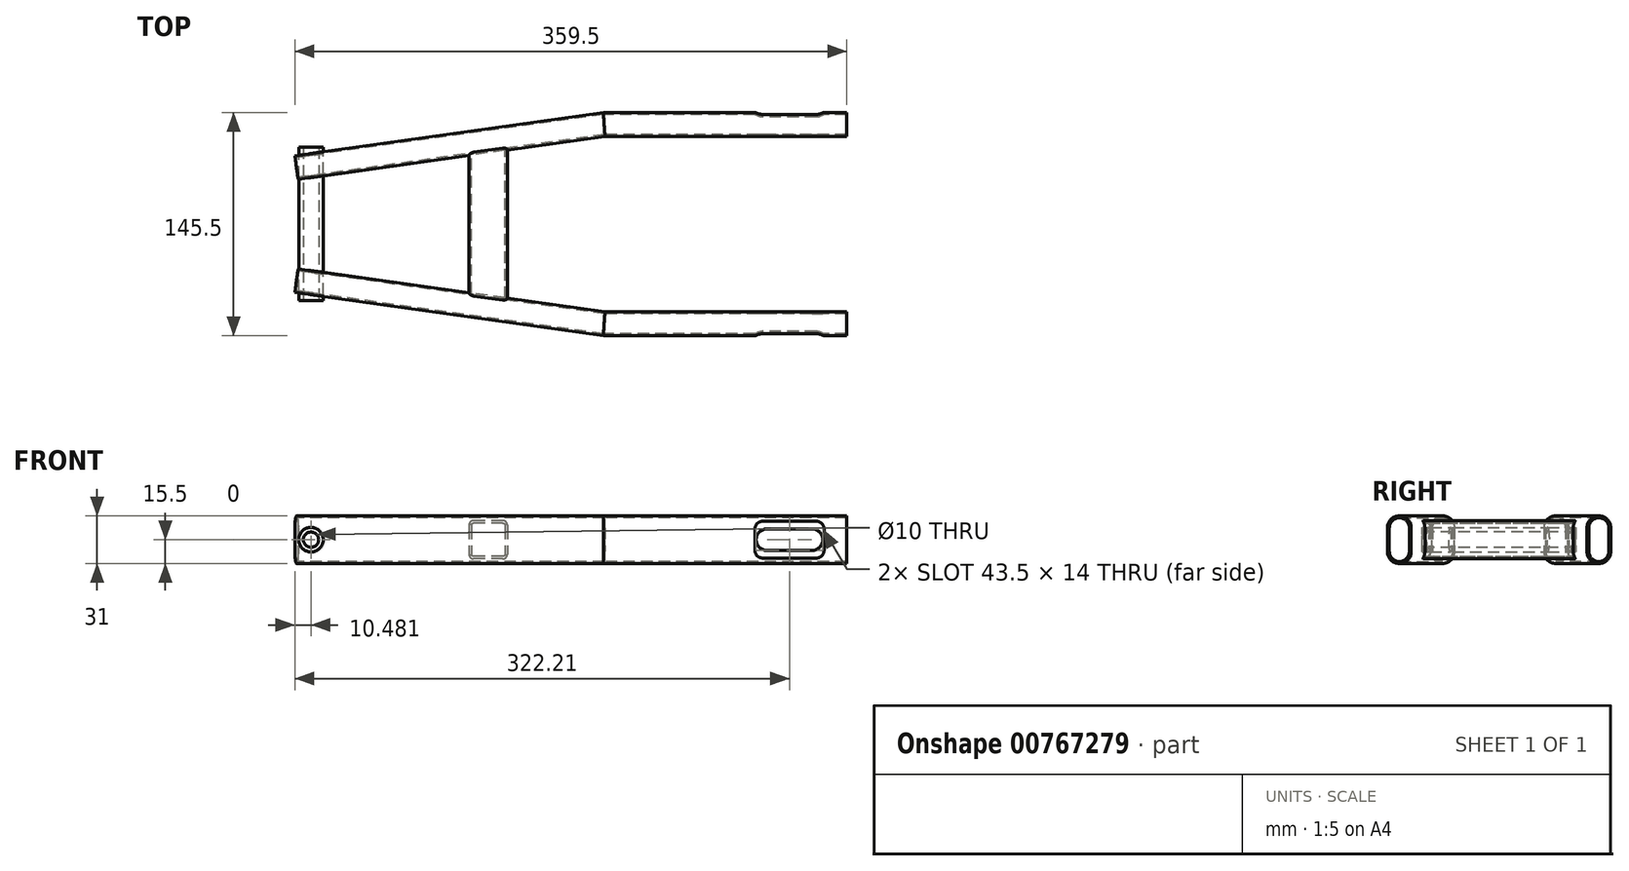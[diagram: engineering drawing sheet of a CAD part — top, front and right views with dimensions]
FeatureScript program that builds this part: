
annotation { "Feature Type Name" : "Feature", "Feature Type Description" : "" }
export const myFeature = defineFeature(function(context is Context, id is Id, definition is map)
    precondition{}
    {
        {
            var Q0;
            Q0=qCreatedBy(makeId("Top.planeOp"),FACE);
            var sketch = newSketch(context, id + "F0", { "sketchPlane" : qUnion([Q0])});
            skLineSegment(sketch, "E0", {"start": v(0, 65) * mm, "end": v(-158.03, 65) * mm});
            skLineSegment(sketch, "E1", {"start": v(-158.03, 65) * mm, "end": v(-358.42, 36.84) * mm});
            skSolve(sketch);
        }
        {
            var Q0;
            Q0=qCreatedBy(makeId("Right.planeOp"),FACE);
            var sketch = newSketch(context, id + "F1", { "sketchPlane" : qUnion([Q0])});
            skLineSegment(sketch, "E2.left", {"start": v(57.25, 7.75) * mm, "end": v(57.25, -7.75) * mm});
            skLineSegment(sketch, "E2.right", {"start": v(72.75, 7.75) * mm, "end": v(72.75, -7.75) * mm});
            skPoint(sketch, "E2.middle", {"position": v(65, 0) * mm});
            skArc(sketch, "E3", {"start": v(57.25, 7.75) * mm, "mid": v(65, 15.5) * mm, "end": v(72.75, 7.75) * mm});
            skArc(sketch, "E4.MirrorCS", {"start": v(57.25, -7.75) * mm, "mid": v(65, -15.5) * mm, "end": v(72.75, -7.75) * mm});
            skLineSegment(sketch, "E5.0", {"start": v(58.45, 7.75) * mm, "end": v(58.45, -7.75) * mm});
            skLineSegment(sketch, "E6.0", {"start": v(71.55, 7.75) * mm, "end": v(71.55, -7.75) * mm});
            skArc(sketch, "E7.0", {"start": v(58.45, 7.75) * mm, "mid": v(65, 14.3) * mm, "end": v(71.55, 7.75) * mm});
            skArc(sketch, "E8.0", {"start": v(58.45, -7.75) * mm, "mid": v(65, -14.3) * mm, "end": v(71.55, -7.75) * mm});
            skSolve(sketch);
        }
        {
            var Q0;
            Q0 = qSketchRegion(id + "F1", true);
            var Q1;
            Q1 = qConstructionFilter(qBodyType(qCreatedBy(id + "F0" ,EDGE), BodyType.WIRE), ConstructionObject.NO);
            sweep(context, id + "F2", {"profiles" : qUnion([Q0]), "path" : qUnion([Q1])});
        }
        {
            var Q0;
            Q0=makeQuery(id+"F2.opSweep","SWEPT_BODY",BODY,{"disambiguationData":[OSD([sQuery(id+"F0.wireOp",EDGE,"E1"),sQuery(id+"F1.wireOp",EDGE,"E2.left"),sQuery(id+"F1.wireOp",EDGE,"E2.right"),sQuery(id+"F1.wireOp",EDGE,"E3"),sQuery(id+"F1.wireOp",EDGE,"E4.MirrorCS"),sQuery(id+"F1.wireOp",EDGE,"E5.0"),sQuery(id+"F1.wireOp",EDGE,"E6.0"),sQuery(id+"F1.wireOp",EDGE,"E7.0"),sQuery(id+"F1.wireOp",EDGE,"E8.0")])]});
            var Q1;
            Q1=qCreatedBy(makeId("Front.planeOp"),FACE);
            mirror(context, id + "F3", {"entities" : qUnion([Q0]), "mirrorPlane" : qUnion([Q1])});
        }
        {
            var Q0;
            Q0=makeQuery(id+"F3.opPattern","COPY",FACE,{"derivedFrom":makeQuery(id+"F2.opSweep","SWEPT_FACE",FACE,{"disambiguationData":[OSD([sQuery(id+"F0.wireOp",EDGE,"E0"),sQuery(id+"F1.wireOp",EDGE,"E2.right")])]}),"instanceName":"1"});
            var sketch = newSketch(context, id + "F4", { "sketchPlane" : qUnion([Q0])});
            skLineSegment(sketch, "E9.bottom", {"start": v(-22.54, -7) * mm, "end": v(-52.04, -7) * mm});
            skLineSegment(sketch, "E9.top", {"start": v(-22.54, 7) * mm, "end": v(-52.04, 7) * mm});
            skPoint(sketch, "E9.middle", {"position": v(-37.3, 0) * mm});
            skArc(sketch, "E10", {"start": v(-22.54, 7) * mm, "mid": v(-15.54, 0) * mm, "end": v(-22.54, -7) * mm});
            skArc(sketch, "E11", {"start": v(-52.04, 7) * mm, "mid": v(-59.04, 0) * mm, "end": v(-52.04, -7) * mm});
            skSolve(sketch);
        }
        {
            var Q0;
            Q0 = qSketchRegion(id + "F4", true);
            extrude(context, id + "F5", {"entities" : qUnion([Q0]), "operationType" : NewBodyOperationType.REMOVE, "endBound" : BoundingType.SYMMETRIC, "oppositeDirection" : true, "depth" : 5000 * mm, "offsetDistance" : 25 * mm});
        }
        {
            var Q0;
            Q0=qCreatedBy(makeId("Front.planeOp"),FACE);
            var sketch = newSketch(context, id + "F6", { "sketchPlane" : qUnion([Q0])});
            skCircle(sketch, "E12", {"center": v(-349.02, 0) * mm, "radius": 8 * mm});
            skSolve(sketch);
        }
        {
            var Q0;
            Q0=makeQuery(id+"F6.imprint","IMPRINT",FACE,{"disambiguationData":[TD([[makeQuery(id+"F6.imprint","IMPRINT",EDGE,{"derivedFrom":sQuery(id+"F6.wireOp",EDGE,"E12")}),1.0]])]});
            extrude(context, id + "F7", {"entities" : qUnion([Q0]), "operationType" : NewBodyOperationType.ADD, "endBound" : BoundingType.SYMMETRIC, "depth" : 100 * mm, "offsetDistance" : 25 * mm});
        }
        {
            var Q0;
            Q0=qCreatedBy(makeId("Front.planeOp"),FACE);
            var sketch = newSketch(context, id + "F8", { "sketchPlane" : qUnion([Q0])});
            skLineSegment(sketch, "E13.bottom", {"start": v(-221.08, -12.5) * mm, "end": v(-246.08, -12.5) * mm});
            skLineSegment(sketch, "E13.top", {"start": v(-221.08, 12.5) * mm, "end": v(-246.08, 12.5) * mm});
            skLineSegment(sketch, "E13.left", {"start": v(-221.08, -12.5) * mm, "end": v(-221.08, 12.5) * mm});
            skLineSegment(sketch, "E13.right", {"start": v(-246.08, -12.5) * mm, "end": v(-246.08, 12.5) * mm});
            skPoint(sketch, "E13.middle", {"position": v(-233.58, 0) * mm});
            skLineSegment(sketch, "E14.0", {"start": v(-224.08, 10.9) * mm, "end": v(-243.08, 10.9) * mm});
            skLineSegment(sketch, "E15.0", {"start": v(-222.68, -9.5) * mm, "end": v(-222.68, 9.5) * mm});
            skLineSegment(sketch, "E16.0", {"start": v(-224.08, -10.9) * mm, "end": v(-243.08, -10.9) * mm});
            skLineSegment(sketch, "E17.0", {"start": v(-244.48, -9.5) * mm, "end": v(-244.48, 9.5) * mm});
            skArc(sketch, "E18.filletArc", {"start": v(-243.08, 10.9) * mm, "mid": v(-244.07, 10.49) * mm, "end": v(-244.48, 9.5) * mm});
            skArc(sketch, "E19.filletArc", {"start": v(-222.68, 9.5) * mm, "mid": v(-223.09, 10.49) * mm, "end": v(-224.08, 10.9) * mm});
            skArc(sketch, "E20.filletArc", {"start": v(-224.08, -10.9) * mm, "mid": v(-223.09, -10.49) * mm, "end": v(-222.68, -9.5) * mm});
            skArc(sketch, "E21.filletArc", {"start": v(-244.48, -9.5) * mm, "mid": v(-244.07, -10.49) * mm, "end": v(-243.08, -10.9) * mm});
            skSolve(sketch);
        }
        {
            var Q0;
            Q0=makeQuery(id+"F4.imprint","IMPRINT",FACE,{"disambiguationData":[TD([[makeQuery(id+"F4.imprint","IMPRINT",EDGE,{"derivedFrom":sQuery(id+"F4.wireOp",EDGE,"E9.bottom")}),-1.0]])]});
            var sketch = newSketch(context, id + "F9", { "sketchPlane" : qUnion([Q0])});
            skLineSegment(sketch, "E22.bottom", {"start": v(-19.76, -12) * mm, "end": v(-54.76, -12) * mm});
            skLineSegment(sketch, "E22.top", {"start": v(-19.76, 12) * mm, "end": v(-54.76, 12) * mm});
            skLineSegment(sketch, "E22.left", {"start": v(-14.76, -7) * mm, "end": v(-14.76, 7) * mm});
            skLineSegment(sketch, "E22.right", {"start": v(-59.76, -7) * mm, "end": v(-59.76, 7) * mm});
            skPoint(sketch, "E22.middle", {"position": v(-37.26, 0) * mm});
            skPoint(sketch, "E23.visualSharp", {"position": v(-59.76, 12) * mm});
            skArc(sketch, "E23.filletArc", {"start": v(-54.76, 12) * mm, "mid": v(-58.3, 10.54) * mm, "end": v(-59.76, 7) * mm});
            skPoint(sketch, "E24.visualSharp", {"position": v(-59.76, -12) * mm});
            skArc(sketch, "E24.filletArc", {"start": v(-59.76, -7) * mm, "mid": v(-58.3, -10.54) * mm, "end": v(-54.76, -12) * mm});
            skPoint(sketch, "E25.visualSharp", {"position": v(-14.76, 12) * mm});
            skArc(sketch, "E25.filletArc", {"start": v(-14.76, 7) * mm, "mid": v(-16.22, 10.54) * mm, "end": v(-19.76, 12) * mm});
            skPoint(sketch, "E26.visualSharp", {"position": v(-14.76, -12) * mm});
            skArc(sketch, "E26.filletArc", {"start": v(-19.76, -12) * mm, "mid": v(-16.22, -10.54) * mm, "end": v(-14.76, -7) * mm});
            skSolve(sketch);
        }
        {
            var Q0;
            Q0=makeQuery(id+"F7.opExtrude","CAP_FACE",FACE,{"disambiguationData":[OSD([sQuery(id+"F6.wireOp",EDGE,"E12")])],"isStart":false});
            var sketch = newSketch(context, id + "F10", { "sketchPlane" : qUnion([Q0])});
            skCircle(sketch, "E27", {"center": v(-349.02, 0) * mm, "radius": 5 * mm});
            skSolve(sketch);
        }
        {
            var Q0;
            Q0=makeQuery(id+"F10.imprint","IMPRINT",FACE,{"disambiguationData":[TD([[makeQuery(id+"F10.imprint","IMPRINT",EDGE,{"derivedFrom":sQuery(id+"F10.wireOp",EDGE,"E27")}),1.0]])]});
            extrude(context, id + "F11", {"entities" : qUnion([Q0]), "operationType" : NewBodyOperationType.REMOVE, "endBound" : BoundingType.THROUGH_ALL, "oppositeDirection" : true, "depth" : 25 * mm, "offsetDistance" : 25 * mm});
        }
        {
            var Q0;
            Q0=makeQuery(id+"F9.imprint","IMPRINT",FACE,{"disambiguationData":[TD([[makeQuery(id+"F9.imprint","IMPRINT",EDGE,{"derivedFrom":sQuery(id+"F9.wireOp",EDGE,"E22.bottom")}),-1.0]])]});
            extrude(context, id + "F12", {"entities" : qUnion([Q0]), "operationType" : NewBodyOperationType.REMOVE, "oppositeDirection" : true, "depth" : 3 * mm, "offsetDistance" : 25 * mm});
        }
        {
            var Q0;
            Q0=makeQuery(id+"F8.imprint","IMPRINT",FACE,{"disambiguationData":[TD([[makeQuery(id+"F8.imprint","IMPRINT",EDGE,{"derivedFrom":sQuery(id+"F8.wireOp",EDGE,"E13.bottom")}),-1.0]])]});
            var Q1;
            Q1=makeQuery(id+"F2.opSweep","SWEPT_BODY",BODY,{"disambiguationData":[OSD([sQuery(id+"F0.wireOp",EDGE,"E1"),sQuery(id+"F1.wireOp",EDGE,"E2.left"),sQuery(id+"F1.wireOp",EDGE,"E2.right"),sQuery(id+"F1.wireOp",EDGE,"E3"),sQuery(id+"F1.wireOp",EDGE,"E4.MirrorCS"),sQuery(id+"F1.wireOp",EDGE,"E5.0"),sQuery(id+"F1.wireOp",EDGE,"E6.0"),sQuery(id+"F1.wireOp",EDGE,"E7.0"),sQuery(id+"F1.wireOp",EDGE,"E8.0")])]});
            extrude(context, id + "F13", {"entities" : qUnion([Q0]), "operationType" : NewBodyOperationType.ADD, "endBound" : BoundingType.UP_TO_BODY, "depth" : 50 * mm, "endBoundEntityBody" : qUnion([Q1]), "offsetDistance" : 25 * mm});
        }
        {
            var Q0;
            Q0=makeQuery(id+"F13.opExtrude","SWEPT_EDGE",EDGE,{"disambiguationData":[OSD([sQuery(id+"F8.wireOp",EDGE,"E13.top"),sQuery(id+"F8.wireOp",EDGE,"E13.left")])]});
            var Q1;
            Q1=makeQuery(id+"F13.opExtrude","SWEPT_EDGE",EDGE,{"disambiguationData":[OSD([sQuery(id+"F8.wireOp",EDGE,"E13.top"),sQuery(id+"F8.wireOp",EDGE,"E13.right")])]});
            var Q2;
            Q2=makeQuery(id+"F13.opExtrude","SWEPT_EDGE",EDGE,{"disambiguationData":[OSD([sQuery(id+"F8.wireOp",EDGE,"E13.bottom"),sQuery(id+"F8.wireOp",EDGE,"E13.left")])]});
            var Q3;
            Q3=makeQuery(id+"F13.opExtrude","SWEPT_EDGE",EDGE,{"disambiguationData":[OSD([sQuery(id+"F8.wireOp",EDGE,"E13.bottom"),sQuery(id+"F8.wireOp",EDGE,"E13.right")])]});
            fillet(context, id + "F14", {"entities" : qUnion([Q0, Q1, Q2, Q3]), "radius" : 3 * mm, "tangentPropagation" : true, "allowEdgeOverflow" : false});
        }
        {
            var Q0;
            Q0=makeQuery(id+"F2.opSweep","SWEPT_BODY",BODY,{"disambiguationData":[OSD([sQuery(id+"F0.wireOp",EDGE,"E1"),sQuery(id+"F1.wireOp",EDGE,"E2.left"),sQuery(id+"F1.wireOp",EDGE,"E2.right"),sQuery(id+"F1.wireOp",EDGE,"E3"),sQuery(id+"F1.wireOp",EDGE,"E4.MirrorCS"),sQuery(id+"F1.wireOp",EDGE,"E5.0"),sQuery(id+"F1.wireOp",EDGE,"E6.0"),sQuery(id+"F1.wireOp",EDGE,"E7.0"),sQuery(id+"F1.wireOp",EDGE,"E8.0")])]});
            var Q1;
            Q1=qCreatedBy(makeId("Front.planeOp"),FACE);
            mirror(context, id + "F15", {"operationType" : NewBodyOperationType.ADD, "entities" : qUnion([Q0]), "mirrorPlane" : qUnion([Q1])});
        }
        {
            var Q0;
            Q0=makeQuery(id+"F9.imprint","IMPRINT",FACE,{"disambiguationData":[TD([[makeQuery(id+"F9.imprint","IMPRINT",EDGE,{"derivedFrom":sQuery(id+"F9.wireOp",EDGE,"E22.bottom")}),-1.0]])]});
            extrude(context, id + "F16", {"entities" : qUnion([Q0]), "operationType" : NewBodyOperationType.REMOVE, "oppositeDirection" : true, "depth" : 3 * mm, "offsetDistance" : 25 * mm});
        }
        {
            var Q0;
            Q0=makeQuery(id+"F2.opSweep","SWEPT_FACE",FACE,{"disambiguationData":[OSD([sQuery(id+"F0.wireOp",EDGE,"E0"),sQuery(id+"F1.wireOp",EDGE,"E2.right")])]});
            var sketch = newSketch(context, id + "F17", { "sketchPlane" : qUnion([Q0])});
            skLineSegment(sketch, "E28.bottom", {"start": v(54.76, 12) * mm, "end": v(19.76, 12) * mm});
            skLineSegment(sketch, "E28.top", {"start": v(54.76, -12) * mm, "end": v(19.76, -12) * mm});
            skLineSegment(sketch, "E28.left", {"start": v(59.76, 7) * mm, "end": v(59.76, -7) * mm});
            skLineSegment(sketch, "E28.right", {"start": v(14.76, 7) * mm, "end": v(14.76, -7) * mm});
            skPoint(sketch, "E28.middle", {"position": v(37.26, 0) * mm});
            skPoint(sketch, "E29.visualSharp", {"position": v(14.76, 12) * mm});
            skArc(sketch, "E29.filletArc", {"start": v(19.76, 12) * mm, "mid": v(16.22, 10.54) * mm, "end": v(14.76, 7) * mm});
            skPoint(sketch, "E30.visualSharp", {"position": v(14.76, -12) * mm});
            skArc(sketch, "E30.filletArc", {"start": v(14.76, -7) * mm, "mid": v(16.22, -10.54) * mm, "end": v(19.76, -12) * mm});
            skPoint(sketch, "E31.visualSharp", {"position": v(59.76, -12) * mm});
            skArc(sketch, "E31.filletArc", {"start": v(54.76, -12) * mm, "mid": v(58.3, -10.54) * mm, "end": v(59.76, -7) * mm});
            skPoint(sketch, "E32.visualSharp", {"position": v(59.76, 12) * mm});
            skArc(sketch, "E32.filletArc", {"start": v(59.76, 7) * mm, "mid": v(58.3, 10.54) * mm, "end": v(54.76, 12) * mm});
            skSolve(sketch);
        }
        {
            var Q0;
            Q0 = qSketchRegion(id + "F17", true);
            extrude(context, id + "F18", {"entities" : qUnion([Q0]), "operationType" : NewBodyOperationType.REMOVE, "oppositeDirection" : true, "depth" : 3 * mm, "offsetDistance" : 25 * mm});
        }
    });
